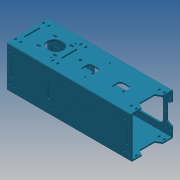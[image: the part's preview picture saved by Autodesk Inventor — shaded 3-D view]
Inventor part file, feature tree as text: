
AUTODESK INVENTOR PART (.ipt)
format: ipt  version: 2017 (Build 210142000, 142)  size: 1,327,104 bytes
history: native  units: mm
features: other x17, sketch x5, extrude x3, projected_geometry x3, plane x1, mirror x1
ambient origin geometry x8: Origin, YZ Plane, XZ Plane, XY Plane, X Axis, Y Axis, Z Axis, Center Point
bodies: Body1 (feature_tree)
feature tree (30):
  other  "Sólido1"
  sketch  "Boceto1"  dims[d1=56.4mm d2=72.0mm]
  extrude  "Extrusión1"  Depth=72.0mm
  other  "Pestaña1"
  other  "Pliegue1"
  other  "Pliegue2"
  sketch  "Boceto4"  dims[d6=8.0mm d8=5.0mm]
  other  "Cara1"
  other  "Cara2"
  extrude  "Extrusión4"  Depth=42.0mm
  sketch  "Boceto5"  dims[d9=41.14mm]
  other  "Cara3"
  plane  "Plano de trabajo1"
  mirror  "Simetría1"
  extrude  "Extrusión5"  Depth=5.0mm
  sketch  "Boceto2"  dims[d4=200.0mm d5=42.0mm]
  other  "Placa1"
  other  "Doblez1"
  other  "Esquina1"
  other  "Placa2"
  other  "Doblez2"
  other  "Placa3"
  other  "Doblez3"
  other  "Placa4"
  other  "Doblez4"
  sketch  "Boceto6"  dims[d10=6.0mm d11=53.14mm d12=6.0mm d13=4.0mm d14=100.0mm d15=20.0mm d16=70.0mm d17=60.0mm d18=4.0mm d19=33.93mm d20=22.0mm d21=120.0mm d22=130.0mm d23=20.0mm d24=4.0mm d25=0.0mm d26=4.0mm d27=2.0mm d28=8.0mm d29=4.0mm d30=120.0mm d31=90.0deg d32=0.1mm d33=16.0mm d34=4.0mm d35=4.0mm d42=47.14mm d43=47.14mm d44=20.0mm d45=6.0mm d46=14.2mm d47=25.0mm d48=0.1mm d49=4.0mm d50=2.0mm d51=8.0mm d52=4.0mm d53=0.1mm d54=4.0mm d55=2.0mm d56=8.0mm d57=4.0mm d58=0.5mm d59=0.5mm d60=20.0mm d61=24.0mm d62=4.4mm d63=41.0mm d70=4.4mm d71=130.8mm d72=25.0mm d73=0.1mm d74=4.0mm d75=2.0mm d76=8.0mm d77=4.0mm d86=50.0mm d87=355.0mm d88=12.5mm d89=12.5mm d90=23.6mm d91=11.8mm d97=190.1mm d102=12.0mm d103=0.25mm d109=12.5mm d113=10.0mm d114=0.0mm d115=10.0mm d116=0.0mm d118=4.0mm d119=5.0mm d120=3.0mm d121=4.0mm d122=5.0mm d123=12.0mm d124=6.0mm d125=24.0mm d126=120.0mm d128=4.0mm d129=2.0mm d130=8.0mm d131=4.0mm d132=90.0deg d133=1.0mm d134=4.0mm d135=2.0mm d136=8.0mm d137=4.0mm d138=90.0deg d139=0.1mm d140=5.0mm d141=90.0mm d142=10.0mm d143=4.0mm d144=80.0mm d145=5.0mm d146=60.0deg d147=55.0mm d148=10.4mm d149=10.4mm d150=4.0mm d151=80.0mm d152=105.5mm d153=10.0mm d154=5.0mm d155=60.0deg d156=41.0mm d157=4.2mm d158=12.5mm]
  projected_geometry  "Contorno proyectado2"
  projected_geometry  "Contorno proyectado3"
  projected_geometry  "Contorno proyectado4"
  other  "Definición1"
